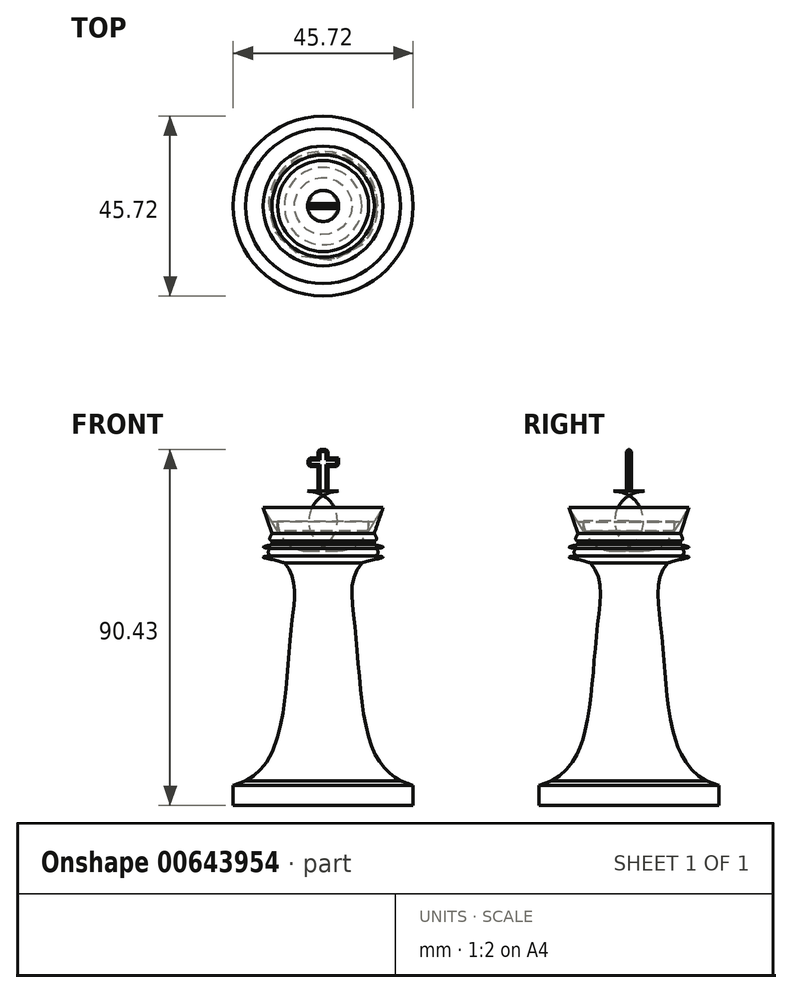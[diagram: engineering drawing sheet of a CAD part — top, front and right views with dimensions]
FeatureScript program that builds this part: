
annotation { "Feature Type Name" : "Feature", "Feature Type Description" : "" }
export const myFeature = defineFeature(function(context is Context, id is Id, definition is map)
    precondition{}
    {
        {
            var Q0;
            Q0=qCreatedBy(makeId("Front.planeOp"),FACE);
            var sketch = newSketch(context, id + "F0", { "sketchPlane" : qUnion([Q0])});
            skLineSegment(sketch, "E0", {"start": v(0, 79.84) * mm, "end": v(0, 60.8) * mm});
            skLineSegment(sketch, "E1", {"start": v(0, 60.8) * mm, "end": v(0, 5.08) * mm});
            skLineSegment(sketch, "E2", {"start": v(22.86, 5.08) * mm, "end": v(22.86, 0) * mm});
            skLineSegment(sketch, "E3", {"start": v(22.86, 0) * mm, "end": v(0, 0) * mm});
            skLineSegment(sketch, "E4", {"start": v(0, 0) * mm, "end": v(0, 5.08) * mm});
            skLineSegment(sketch, "E5", {"start": v(13, 65.33) * mm, "end": v(13, 69.14) * mm});
            skLineSegment(sketch, "E6", {"start": v(13.4, 64.6) * mm, "end": v(31.84, 64.6) * mm, "construction": true});
            skLineSegment(sketch, "E7", {"start": v(10.14, 69.08) * mm, "end": v(10.14, 71.62) * mm, "construction": true});
            skLineSegment(sketch, "E8", {"start": v(11.58, 69.14) * mm, "end": v(11.58, 79.84) * mm});
            skLineSegment(sketch, "E9", {"start": v(11.58, 79.84) * mm, "end": v(0, 79.84) * mm});
            skArc(sketch, "E10", {"start": v(12.95, 63.4) * mm, "mid": v(13.96, 64.34) * mm, "end": v(13, 65.33) * mm});
            skFitSpline(sketch, "E11", {"points": [v(12.95, 63.4) * mm, v(15.22, 63.08) * mm, v(9.84, 61.58) * mm], "startDerivative": vector(7.01, -0.16) * mm, "endDerivative": vector(-7.06, -3.42) * mm});
            skLineSegment(sketch, "E12", {"start": v(13, 64.36) * mm, "end": v(13.96, 64.36) * mm, "construction": true});
            skFitSpline(sketch, "E13.MirrorCS", {"points": [v(12.95, 65.33) * mm, v(15.22, 65.65) * mm, v(9.84, 67.15) * mm], "startDerivative": vector(7.01, 0.16) * mm, "endDerivative": vector(-7.06, 3.42) * mm});
            skPoint(sketch, "E14.2.internal.snap0", {"position": v(13, 67.24) * mm});
            skFitSpline(sketch, "E14", {"points": [v(13, 69.14) * mm, v(13.56, 67.6) * mm, v(13, 67.15) * mm], "startDerivative": vector(1.66, -3) * mm, "endDerivative": vector(-1.9, -0.85) * mm});
            skLineSegment(sketch, "E15", {"start": v(13, 69.14) * mm, "end": v(15.22, 75.65) * mm});
            skLineSegment(sketch, "E16", {"start": v(15.22, 75.65) * mm, "end": v(13, 72.08) * mm});
            skLineSegment(sketch, "E17", {"start": v(13, 72.08) * mm, "end": v(11.58, 69.68) * mm});
            skFitSpline(sketch, "E18", {"points": [v(19.67, 6.25) * mm, v(12.25, 15.23) * mm, v(8.15, 44.55) * mm, v(9.84, 61.58) * mm], "startDerivative": vector(-33.9, 18.68) * mm, "endDerivative": vector(35.13, 37.53) * mm});
            skLineSegment(sketch, "E19", {"start": v(22.86, 5.08) * mm, "end": v(19.67, 6.25) * mm});
            skSolve(sketch);
        }
        {
            var Q0;
            {var subQ0=sQuery(id+"F0.wireOp",EDGE,"b5c3ff92-521e-4655-9f4a-06a43d0b36a7");Q0=makeQuery(id+"F0.imprint","IMPRINT",FACE,{"disambiguationData":[TD([[makeQuery(id+"F0.imprint","IMPRINT",EDGE,{"derivedFrom":subQ0}),1.0]])]});}
            var Q1;
            {var subQ9=sQuery(id+"F0.wireOp",EDGE,"E1");Q1=makeQuery(id+"F0.imprint","IMPRINT",FACE,{"disambiguationData":[TD([[makeQuery(id+"F0.imprint","IMPRINT",EDGE,{"derivedFrom":subQ9}),1.0]])]});}
            var Q2;
            {var subQ0=sQuery(id+"F0.wireOp",EDGE,"E13.MirrorCS");var subQ1=sQuery(id+"F0.wireOp",EDGE,"E5");var subQ3=makeQuery(id+"F0.imprint","INTERSECT",VERTEX,{"derivedFrom":[subQ1,subQ0]});Q2=makeQuery(id+"F0.imprint","IMPRINT",FACE,{"disambiguationData":[TD([[makeQuery(id+"F0.imprint","IMPRINT",EDGE,{"disambiguationData":[TD([[subQ3,1.0]])],"derivedFrom":subQ1}),-1.0]])]});}
            var Q3;
            {var subQ0=sQuery(id+"F0.wireOp",EDGE,"E14");Q3=makeQuery(id+"F0.imprint","IMPRINT",FACE,{"disambiguationData":[TD([[makeQuery(id+"F0.imprint","IMPRINT",EDGE,{"derivedFrom":subQ0}),-1.0]])]});}
            var Q4;
            {var subQ0=sQuery(id+"F0.wireOp",EDGE,"E10");Q4=makeQuery(id+"F0.imprint","IMPRINT",FACE,{"disambiguationData":[TD([[makeQuery(id+"F0.imprint","IMPRINT",EDGE,{"derivedFrom":subQ0}),1.0]])]});}
            var Q5;
            {var subQ0=sQuery(id+"F0.wireOp",EDGE,"E11");var subQ1=sQuery(id+"F0.wireOp",EDGE,"e2eccbfb-57c4-43df-9bc5-db1abbeb1765");var subQ2=makeQuery(id+"F0.imprint","INTERSECT",VERTEX,{"disambiguationData":[OD(0.0)],"derivedFrom":[subQ1,subQ0]});Q5=makeQuery(id+"F0.imprint","IMPRINT",FACE,{"disambiguationData":[TD([[makeQuery(id+"F0.imprint","IMPRINT",EDGE,{"disambiguationData":[TD([[subQ2,1.0]])],"derivedFrom":subQ1}),-1.0]])]});}
            var Q6;
            Q6=sQuery(id+"F0.wireOp",EDGE,"E0");
            revolve(context, id + "F1", {"surfaceOperationType" : NewSurfaceOperationType.NEW, "entities" : qUnion([Q0, Q1, Q2, Q3, Q4, Q5]), "axis" : qUnion([Q6]), "revolveType" : RevolveType.FULL});
        }
        {
            var Q0;
            Q0=makeQuery(id+"F1.opRevolve","SWEPT_FACE",FACE,{"disambiguationData":[OSD([sQuery(id+"F0.wireOp",EDGE,"E9")])]});
            fillet(context, id + "F2", {"entities" : qUnion([Q0]), "radius" : 7.62 * mm, "tangentPropagation" : true, "allowEdgeOverflow" : false});
        }
        {
            var Q0;
            Q0=qCreatedBy(makeId("Front.planeOp"),FACE);
            var sketch = newSketch(context, id + "F3", { "sketchPlane" : qUnion([Q0])});
            skLineSegment(sketch, "E20", {"start": v(0, 79.84) * mm, "end": v(0, 75.65) * mm, "construction": true});
            skLineSegment(sketch, "E21", {"start": v(0, 79.84) * mm, "end": v(1.27, 79.84) * mm});
            skLineSegment(sketch, "E22.MirrorCS", {"start": v(0, 79.84) * mm, "end": v(-1.27, 79.84) * mm});
            skLineSegment(sketch, "E23", {"start": v(1.27, 79.84) * mm, "end": v(1.27, 86.13) * mm});
            skLineSegment(sketch, "E24", {"start": v(1.27, 86.13) * mm, "end": v(3.85, 86.13) * mm});
            skLineSegment(sketch, "E25", {"start": v(3.85, 86.13) * mm, "end": v(3.85, 88.22) * mm});
            skLineSegment(sketch, "E26", {"start": v(3.85, 88.22) * mm, "end": v(1.27, 88.22) * mm});
            skLineSegment(sketch, "E27", {"start": v(1.27, 88.22) * mm, "end": v(1.27, 90.43) * mm});
            skLineSegment(sketch, "E28", {"start": v(1.27, 90.43) * mm, "end": v(0, 90.43) * mm});
            skLineSegment(sketch, "E29.MirrorCS", {"start": v(-1.27, 79.84) * mm, "end": v(-1.27, 86.13) * mm});
            skLineSegment(sketch, "E30.MirrorCS", {"start": v(-1.27, 86.13) * mm, "end": v(-3.85, 86.13) * mm});
            skLineSegment(sketch, "E31.MirrorCS", {"start": v(-3.85, 86.13) * mm, "end": v(-3.85, 88.22) * mm});
            skLineSegment(sketch, "E32.MirrorCS", {"start": v(-3.85, 88.22) * mm, "end": v(-1.27, 88.22) * mm});
            skLineSegment(sketch, "E33.MirrorCS", {"start": v(-1.27, 90.43) * mm, "end": v(0, 90.43) * mm});
            skLineSegment(sketch, "E34.MirrorCS", {"start": v(-1.27, 88.22) * mm, "end": v(-1.27, 90.43) * mm});
            skSolve(sketch);
        }
        {
            var Q0;
            Q0=makeQuery(id+"F3.imprint","IMPRINT",FACE,{"disambiguationData":[TD([[makeQuery(id+"F3.imprint","IMPRINT",EDGE,{"derivedFrom":sQuery(id+"F3.wireOp",EDGE,"E21")}),1.0]])]});
            extrude(context, id + "F4", {"entities" : qUnion([Q0]), "operationType" : NewBodyOperationType.ADD, "depth" : 1.27 * mm, "offsetDistance" : 25.4 * mm, "symmetric" : true});
        }
        {
            var Q0;
            Q0=makeQuery(id+"F4.opExtrude","CAP_EDGE",EDGE,{"disambiguationData":[OSD([sQuery(id+"F3.wireOp",EDGE,"E28"),sQuery(id+"F3.wireOp",EDGE,"E33.MirrorCS")])],"isStart":false});
            var Q1;
            Q1=makeQuery(id+"F4.opExtrude","CAP_EDGE",EDGE,{"disambiguationData":[OSD([sQuery(id+"F3.wireOp",EDGE,"E28"),sQuery(id+"F3.wireOp",EDGE,"E33.MirrorCS")])],"isStart":true});
            var Q2;
            Q2=makeQuery(id+"F4.opExtrude","SWEPT_EDGE",EDGE,{"disambiguationData":[OSD([sQuery(id+"F3.wireOp",EDGE,"E33.MirrorCS"),sQuery(id+"F3.wireOp",EDGE,"E34.MirrorCS")])]});
            var Q3;
            Q3=makeQuery(id+"F4.opExtrude","SWEPT_EDGE",EDGE,{"disambiguationData":[OSD([sQuery(id+"F3.wireOp",EDGE,"E27"),sQuery(id+"F3.wireOp",EDGE,"E28")])]});
            var Q4;
            Q4=makeQuery(id+"F4.opExtrude","CAP_EDGE",EDGE,{"disambiguationData":[OSD([sQuery(id+"F3.wireOp",EDGE,"E27")])],"isStart":false});
            var Q5;
            Q5=makeQuery(id+"F4.opExtrude","CAP_EDGE",EDGE,{"disambiguationData":[OSD([sQuery(id+"F3.wireOp",EDGE,"E27")])],"isStart":true});
            var Q6;
            Q6=makeQuery(id+"F4.opExtrude","CAP_EDGE",EDGE,{"disambiguationData":[OSD([sQuery(id+"F3.wireOp",EDGE,"E26")])],"isStart":true});
            var Q7;
            Q7=makeQuery(id+"F4.opExtrude","CAP_EDGE",EDGE,{"disambiguationData":[OSD([sQuery(id+"F3.wireOp",EDGE,"E34.MirrorCS")])],"isStart":true});
            var Q8;
            Q8=makeQuery(id+"F4.opExtrude","CAP_EDGE",EDGE,{"disambiguationData":[OSD([sQuery(id+"F3.wireOp",EDGE,"E34.MirrorCS")])],"isStart":false});
            var Q9;
            Q9=makeQuery(id+"F4.opExtrude","CAP_EDGE",EDGE,{"disambiguationData":[OSD([sQuery(id+"F3.wireOp",EDGE,"E32.MirrorCS")])],"isStart":true});
            var Q10;
            Q10=makeQuery(id+"F4.opExtrude","CAP_EDGE",EDGE,{"disambiguationData":[OSD([sQuery(id+"F3.wireOp",EDGE,"E32.MirrorCS")])],"isStart":false});
            var Q11;
            Q11=makeQuery(id+"F4.opExtrude","SWEPT_EDGE",EDGE,{"disambiguationData":[OSD([sQuery(id+"F3.wireOp",EDGE,"E31.MirrorCS"),sQuery(id+"F3.wireOp",EDGE,"E32.MirrorCS")])]});
            var Q12;
            Q12=makeQuery(id+"F4.opExtrude","CAP_EDGE",EDGE,{"disambiguationData":[OSD([sQuery(id+"F3.wireOp",EDGE,"E31.MirrorCS")])],"isStart":true});
            var Q13;
            Q13=makeQuery(id+"F4.opExtrude","CAP_EDGE",EDGE,{"disambiguationData":[OSD([sQuery(id+"F3.wireOp",EDGE,"E31.MirrorCS")])],"isStart":false});
            var Q14;
            Q14=makeQuery(id+"F4.opExtrude","SWEPT_EDGE",EDGE,{"disambiguationData":[OSD([sQuery(id+"F3.wireOp",EDGE,"E30.MirrorCS"),sQuery(id+"F3.wireOp",EDGE,"E31.MirrorCS")])]});
            var Q15;
            Q15=makeQuery(id+"F4.opExtrude","CAP_EDGE",EDGE,{"disambiguationData":[OSD([sQuery(id+"F3.wireOp",EDGE,"E25")])],"isStart":false});
            var Q16;
            Q16=makeQuery(id+"F4.opExtrude","CAP_EDGE",EDGE,{"disambiguationData":[OSD([sQuery(id+"F3.wireOp",EDGE,"E26")])],"isStart":false});
            var Q17;
            Q17=makeQuery(id+"F4.opExtrude","CAP_EDGE",EDGE,{"disambiguationData":[OSD([sQuery(id+"F3.wireOp",EDGE,"E25")])],"isStart":true});
            var Q18;
            Q18=makeQuery(id+"F4.opExtrude","SWEPT_EDGE",EDGE,{"disambiguationData":[OSD([sQuery(id+"F3.wireOp",EDGE,"E24"),sQuery(id+"F3.wireOp",EDGE,"E25")])]});
            var Q19;
            Q19=makeQuery(id+"F4.opExtrude","CAP_EDGE",EDGE,{"disambiguationData":[OSD([sQuery(id+"F3.wireOp",EDGE,"E30.MirrorCS")])],"isStart":false});
            var Q20;
            Q20=makeQuery(id+"F4.opExtrude","CAP_EDGE",EDGE,{"disambiguationData":[OSD([sQuery(id+"F3.wireOp",EDGE,"E30.MirrorCS")])],"isStart":true});
            var Q21;
            Q21=makeQuery(id+"F4.opExtrude","CAP_EDGE",EDGE,{"disambiguationData":[OSD([sQuery(id+"F3.wireOp",EDGE,"E29.MirrorCS")])],"isStart":false});
            var Q22;
            Q22=makeQuery(id+"F4.opExtrude","CAP_EDGE",EDGE,{"disambiguationData":[OSD([sQuery(id+"F3.wireOp",EDGE,"E29.MirrorCS")])],"isStart":true});
            var Q23;
            Q23=makeQuery(id+"F4.opExtrude","CAP_EDGE",EDGE,{"disambiguationData":[OSD([sQuery(id+"F3.wireOp",EDGE,"E23")])],"isStart":true});
            var Q24;
            Q24=makeQuery(id+"F4.opExtrude","CAP_EDGE",EDGE,{"disambiguationData":[OSD([sQuery(id+"F3.wireOp",EDGE,"E23")])],"isStart":false});
            var Q25;
            Q25=makeQuery(id+"F4.opExtrude","CAP_EDGE",EDGE,{"disambiguationData":[OSD([sQuery(id+"F3.wireOp",EDGE,"E24")])],"isStart":false});
            var Q26;
            Q26=makeQuery(id+"F4.opExtrude","CAP_EDGE",EDGE,{"disambiguationData":[OSD([sQuery(id+"F3.wireOp",EDGE,"E24")])],"isStart":true});
            chamfer(context, id + "F5", {"entities" : qUnion([Q0, Q1, Q2, Q3, Q4, Q5, Q6, Q7, Q8, Q9, Q10, Q11, Q12, Q13, Q14, Q15, Q16, Q17, Q18, Q19, Q20, Q21, Q22, Q23, Q24, Q25, Q26]), "width" : 0.5 * mm, "tangentPropagation" : true});
        }
    });
